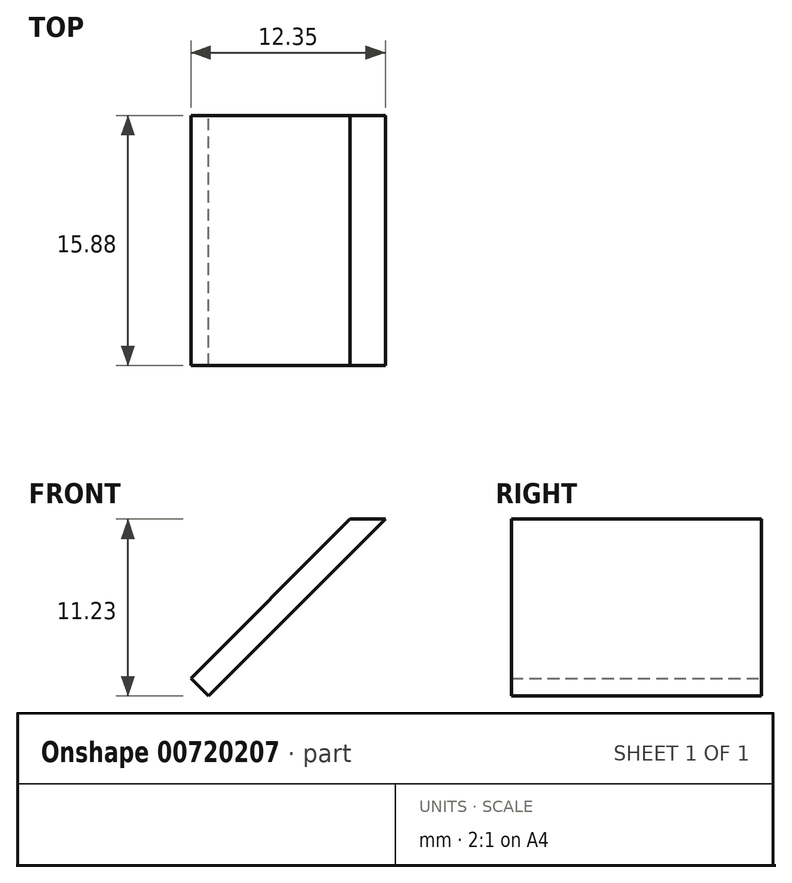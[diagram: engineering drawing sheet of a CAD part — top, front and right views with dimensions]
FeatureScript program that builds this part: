
annotation { "Feature Type Name" : "Feature", "Feature Type Description" : "" }
export const myFeature = defineFeature(function(context is Context, id is Id, definition is map)
    precondition{}
    {
        {
            var Q0;
            Q0=qCreatedBy(makeId("Front.planeOp"),FACE);
            var sketch = newSketch(context, id + "F0", { "sketchPlane" : qUnion([Q0])});
            skLineSegment(sketch, "E0", {"start": v(0, 0) * mm, "end": v(-10.1, -10.1) * mm});
            skLineSegment(sketch, "E1", {"start": v(-10.1, -10.1) * mm, "end": v(-8.98, -11.23) * mm});
            skLineSegment(sketch, "E2", {"start": v(-8.98, -11.23) * mm, "end": v(2.25, 0) * mm});
            skLineSegment(sketch, "E3", {"start": v(2.25, 0) * mm, "end": v(0, 0) * mm});
            skSolve(sketch);
        }
        {
            var Q0;
            Q0=makeQuery(id+"F0.imprint","IMPRINT",FACE,{"disambiguationData":[TD([[makeQuery(id+"F0.imprint","IMPRINT",EDGE,{"derivedFrom":sQuery(id+"F0.wireOp",EDGE,"E0")}),1.0]])]});
            extrude(context, id + "F1", {"entities" : qUnion([Q0]), "depth" : 15.88 * mm});
        }
    });
